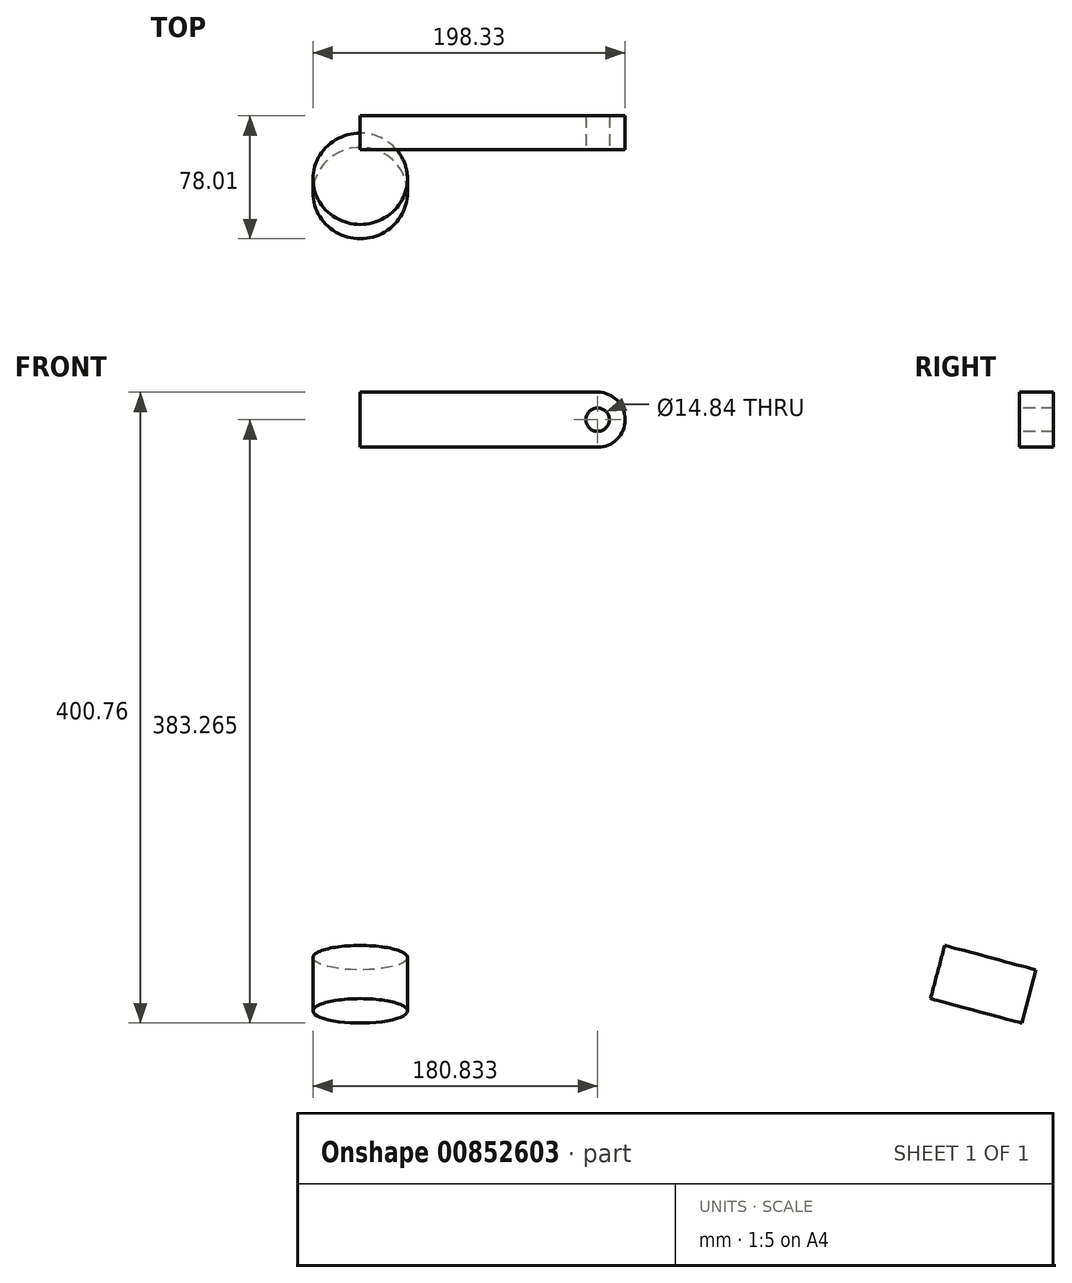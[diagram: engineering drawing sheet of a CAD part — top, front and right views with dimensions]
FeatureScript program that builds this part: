
annotation { "Feature Type Name" : "Feature", "Feature Type Description" : "" }
export const myFeature = defineFeature(function(context is Context, id is Id, definition is map)
    precondition{}
    {
        {
            var Q0;
            Q0=qCreatedBy(makeId("Front.planeOp"),FACE);
            var sketch = newSketch(context, id + "F0", { "sketchPlane" : qUnion([Q0])});
            skCircle(sketch, "E0", {"center": v(72.5, 0) * mm, "radius": 15 * mm});
            skCircle(sketch, "E1", {"center": v(95, 140) * mm, "radius": 15 * mm});
            skLineSegment(sketch, "E2.bottom", {"start": v(72.5, 15) * mm, "end": v(0, 15) * mm});
            skLineSegment(sketch, "E2.top", {"start": v(72.5, -15) * mm, "end": v(0, -15) * mm});
            skLineSegment(sketch, "E2.left", {"start": v(72.5, 15) * mm, "end": v(72.5, -15) * mm});
            skLineSegment(sketch, "E2.right", {"start": v(0, 15) * mm, "end": v(0, -15) * mm});
            skLineSegment(sketch, "E3.bottom", {"start": v(94.96, 125) * mm, "end": v(0, 125) * mm});
            skLineSegment(sketch, "E3.top", {"start": v(94.96, 155) * mm, "end": v(0, 155) * mm});
            skLineSegment(sketch, "E3.left", {"start": v(94.96, 155) * mm, "end": v(94.96, 125) * mm});
            skLineSegment(sketch, "E3.right", {"start": v(0, 155) * mm, "end": v(0, 125) * mm});
            skSolve(sketch);
        }
        {
            var Q0;
            {var subQ1=sQuery(id+"F0.wireOp",EDGE,"E3.bottom");Q0=makeQuery(id+"F0.imprint","IMPRINT",FACE,{"disambiguationData":[TD([[makeQuery(id+"F0.imprint","IMPRINT",EDGE,{"derivedFrom":subQ1}),1.0]])]});}
            var Q1;
            {var subQ4=sQuery(id+"F0.wireOp",EDGE,"E2.bottom");Q1=makeQuery(id+"F0.imprint","IMPRINT",FACE,{"disambiguationData":[TD([[makeQuery(id+"F0.imprint","IMPRINT",EDGE,{"derivedFrom":subQ4}),1.0]])]});}
            var Q2;
            {var subQ0=sQuery(id+"F0.wireOp",EDGE,"E3.left");var subQ1=sQuery(id+"F0.wireOp",EDGE,"E1");var subQ3=makeQuery(id+"F0.imprint","INTERSECT",VERTEX,{"derivedFrom":[subQ1,subQ0]});Q2=makeQuery(id+"F0.imprint","IMPRINT",FACE,{"disambiguationData":[TD([[makeQuery(id+"F0.imprint","IMPRINT",EDGE,{"disambiguationData":[TD([[subQ3,1.0]])],"derivedFrom":subQ1}),1.0]])]});}
            var Q3;
            {var subQ0=sQuery(id+"F0.wireOp",EDGE,"E3.left");var subQ1=sQuery(id+"F0.wireOp",EDGE,"E1");var subQ3=makeQuery(id+"F0.imprint","INTERSECT",VERTEX,{"derivedFrom":[subQ1,subQ0]});Q3=makeQuery(id+"F0.imprint","IMPRINT",FACE,{"disambiguationData":[TD([[makeQuery(id+"F0.imprint","IMPRINT",EDGE,{"disambiguationData":[TD([[subQ3,-1.0]])],"derivedFrom":subQ1}),1.0]])]});}
            var Q4;
            {var subQ0=sQuery(id+"F0.wireOp",EDGE,"E2.left");var subQ1=sQuery(id+"F0.wireOp",EDGE,"E0");var subQ3=makeQuery(id+"F0.imprint","INTERSECT",VERTEX,{"derivedFrom":[subQ1,subQ0]});Q4=makeQuery(id+"F0.imprint","IMPRINT",FACE,{"disambiguationData":[TD([[makeQuery(id+"F0.imprint","IMPRINT",EDGE,{"disambiguationData":[TD([[subQ3,1.0]])],"derivedFrom":subQ1}),1.0]])]});}
            var Q5;
            {var subQ0=sQuery(id+"F0.wireOp",EDGE,"E2.left");var subQ1=sQuery(id+"F0.wireOp",EDGE,"E0");var subQ3=makeQuery(id+"F0.imprint","INTERSECT",VERTEX,{"derivedFrom":[subQ1,subQ0]});Q5=makeQuery(id+"F0.imprint","IMPRINT",FACE,{"disambiguationData":[TD([[makeQuery(id+"F0.imprint","IMPRINT",EDGE,{"disambiguationData":[TD([[subQ3,-1.0]])],"derivedFrom":subQ1}),1.0]])]});}
            var Q6;
            {var subQ1=sQuery(id+"F0.wireOp",EDGE,"E3.bottom");Q6=makeQuery(id+"F0.imprint","IMPRINT",FACE,{"disambiguationData":[TD([[makeQuery(id+"F0.imprint","IMPRINT",EDGE,{"derivedFrom":subQ1}),-1.0]])]});}
            extrude(context, id + "F1", {"entities" : qUnion([Q0, Q1, Q2, Q3, Q4, Q5, Q6]), "depth" : 54 * mm, "offsetDistance" : 25 * mm});
        }
        {
            var Q0;
            {var subQ1=sQuery(id+"F0.wireOp",EDGE,"E3.bottom");Q0=makeQuery(id+"F0.imprint","IMPRINT",FACE,{"disambiguationData":[TD([[makeQuery(id+"F0.imprint","IMPRINT",EDGE,{"derivedFrom":subQ1}),1.0]])]});}
            var Q1;
            {var subQ0=sQuery(id+"F0.wireOp",EDGE,"E3.left");var subQ1=sQuery(id+"F0.wireOp",EDGE,"E1");var subQ3=makeQuery(id+"F0.imprint","INTERSECT",VERTEX,{"derivedFrom":[subQ1,subQ0]});Q1=makeQuery(id+"F0.imprint","IMPRINT",FACE,{"disambiguationData":[TD([[makeQuery(id+"F0.imprint","IMPRINT",EDGE,{"disambiguationData":[TD([[subQ3,1.0]])],"derivedFrom":subQ1}),1.0]])]});}
            var Q2;
            {var subQ0=sQuery(id+"F0.wireOp",EDGE,"E3.left");var subQ1=sQuery(id+"F0.wireOp",EDGE,"E1");var subQ3=makeQuery(id+"F0.imprint","INTERSECT",VERTEX,{"derivedFrom":[subQ1,subQ0]});Q2=makeQuery(id+"F0.imprint","IMPRINT",FACE,{"disambiguationData":[TD([[makeQuery(id+"F0.imprint","IMPRINT",EDGE,{"disambiguationData":[TD([[subQ3,-1.0]])],"derivedFrom":subQ1}),1.0]])]});}
            var Q3;
            {var subQ1=sQuery(id+"F0.wireOp",EDGE,"E3.bottom");Q3=makeQuery(id+"F0.imprint","IMPRINT",FACE,{"disambiguationData":[TD([[makeQuery(id+"F0.imprint","IMPRINT",EDGE,{"derivedFrom":subQ1}),-1.0]])]});}
            extrude(context, id + "F2", {"entities" : qUnion([Q0, Q1, Q2, Q3]), "oppositeDirection" : true, "depth" : 135 * mm, "offsetDistance" : 25 * mm});
        }
        {
            var Q0;
            {var subQ4=sQuery(id+"F0.wireOp",EDGE,"E2.bottom");Q0=makeQuery(id+"F0.imprint","IMPRINT",FACE,{"disambiguationData":[TD([[makeQuery(id+"F0.imprint","IMPRINT",EDGE,{"derivedFrom":subQ4}),1.0]])]});}
            var Q1;
            {var subQ0=sQuery(id+"F0.wireOp",EDGE,"E2.left");var subQ1=sQuery(id+"F0.wireOp",EDGE,"E0");var subQ3=makeQuery(id+"F0.imprint","INTERSECT",VERTEX,{"derivedFrom":[subQ1,subQ0]});Q1=makeQuery(id+"F0.imprint","IMPRINT",FACE,{"disambiguationData":[TD([[makeQuery(id+"F0.imprint","IMPRINT",EDGE,{"disambiguationData":[TD([[subQ3,1.0]])],"derivedFrom":subQ1}),1.0]])]});}
            var Q2;
            {var subQ0=sQuery(id+"F0.wireOp",EDGE,"E2.left");var subQ1=sQuery(id+"F0.wireOp",EDGE,"E0");var subQ3=makeQuery(id+"F0.imprint","INTERSECT",VERTEX,{"derivedFrom":[subQ1,subQ0]});Q2=makeQuery(id+"F0.imprint","IMPRINT",FACE,{"disambiguationData":[TD([[makeQuery(id+"F0.imprint","IMPRINT",EDGE,{"disambiguationData":[TD([[subQ3,-1.0]])],"derivedFrom":subQ1}),1.0]])]});}
            extrude(context, id + "F3", {"entities" : qUnion([Q0, Q1, Q2]), "oppositeDirection" : true, "depth" : 142 * mm, "offsetDistance" : 25 * mm});
        }
        {
            var Q0;
            Q0=makeQuery(id+"F2.opExtrude","CAP_FACE",FACE,{"disambiguationData":[OSD([sQuery(id+"F0.wireOp",EDGE,"E1"),sQuery(id+"F0.wireOp",EDGE,"E3.bottom"),sQuery(id+"F0.wireOp",EDGE,"E3.top"),sQuery(id+"F0.wireOp",EDGE,"E3.left"),sQuery(id+"F0.wireOp",EDGE,"E3.right")])],"isStart":false});
            extrude(context, id + "F4", {"entities" : qUnion([Q0]), "depth" : 54 * mm, "offsetDistance" : 25 * mm});
        }
        {
            var Q0;
            Q0=makeQuery(id+"F3.opExtrude","CAP_FACE",FACE,{"disambiguationData":[OSD([sQuery(id+"F0.wireOp",EDGE,"E0"),sQuery(id+"F0.wireOp",EDGE,"E2.bottom"),sQuery(id+"F0.wireOp",EDGE,"E2.top"),sQuery(id+"F0.wireOp",EDGE,"E2.left"),sQuery(id+"F0.wireOp",EDGE,"E2.right")])],"isStart":false});
            extrude(context, id + "F5", {"entities" : qUnion([Q0]), "depth" : 54 * mm, "offsetDistance" : 25 * mm});
        }
        {
            var Q0;
            Q0=qCreatedBy(makeId("Right.planeOp"),FACE);
            var sketch = newSketch(context, id + "F6", { "sketchPlane" : qUnion([Q0])});
            skLineSegment(sketch, "E4.bottom", {"start": v(81.76, 361.74) * mm, "end": v(60.24, 361.74) * mm});
            skLineSegment(sketch, "E4.top", {"start": v(81.76, 403.26) * mm, "end": v(60.24, 403.26) * mm});
            skLineSegment(sketch, "E4.left", {"start": v(81.76, 361.74) * mm, "end": v(81.76, 403.26) * mm});
            skLineSegment(sketch, "E4.right", {"start": v(60.24, 361.74) * mm, "end": v(60.24, 403.26) * mm});
            skPoint(sketch, "E4.middle", {"position": v(71, 382.5) * mm});
            skSolve(sketch);
        }
        {
            var Q0;
            Q0=makeQuery(id+"F6.imprint","IMPRINT",FACE,{"disambiguationData":[TD([[makeQuery(id+"F6.imprint","IMPRINT",EDGE,{"derivedFrom":sQuery(id+"F6.wireOp",EDGE,"E4.bottom")}),-1.0]])]});
            extrude(context, id + "F7", {"entities" : qUnion([Q0]), "depth" : 169 * mm, "offsetDistance" : 25 * mm});
        }
        {
            var Q0;
            Q0=makeQuery(id+"F7.opExtrude","SWEPT_FACE",FACE,{"disambiguationData":[OSD([sQuery(id+"F6.wireOp",EDGE,"E4.right")])]});
            var sketch = newSketch(context, id + "F8", { "sketchPlane" : qUnion([Q0])});
            skCircle(sketch, "E5", {"center": v(150.83, 381.74) * mm, "radius": 17.5 * mm});
            skCircle(sketch, "E6", {"center": v(150.83, 381.74) * mm, "radius": 7.42 * mm});
            skLineSegment(sketch, "E7.bottom", {"start": v(150.92, 399.23) * mm, "end": v(-0.78, 399.23) * mm});
            skLineSegment(sketch, "E7.top", {"start": v(150.92, 364.24) * mm, "end": v(-0.78, 364.24) * mm});
            skLineSegment(sketch, "E7.left", {"start": v(150.92, 399.23) * mm, "end": v(150.92, 364.24) * mm});
            skLineSegment(sketch, "E7.right", {"start": v(-0.78, 399.23) * mm, "end": v(-0.78, 364.24) * mm});
            skSolve(sketch);
        }
        {
            var Q0;
            {var subQ1=makeQuery(id+"F7.opExtrude","CAP_EDGE",EDGE,{"disambiguationData":[OSD([sQuery(id+"F6.wireOp",EDGE,"E4.right")])],"isStart":false});var subQ4=sQuery(id+"F8.wireOp",EDGE,"E6");var subQ5=makeQuery(id+"F8.imprint","INTERSECT",VERTEX,{"disambiguationData":[OD(0.0)],"derivedFrom":[subQ1,subQ4]});Q0=makeQuery(id+"F8.imprint","IMPRINT",FACE,{"disambiguationData":[TD([[makeQuery(id+"F8.imprint","IMPRINT",EDGE,{"disambiguationData":[TD([[subQ5,-1.0]])],"derivedFrom":subQ4}),-1.0]])]});}
            var Q1;
            {var subQ0=sQuery(id+"F8.wireOp",EDGE,"2KteYOMI-rCw2-rHk1-Q1Dc-6oNoVVmJXsEm");Q1=makeQuery(id+"F8.imprint","IMPRINT",FACE,{"disambiguationData":[TD([[makeQuery(id+"F8.imprint","IMPRINT",EDGE,{"derivedFrom":subQ0}),1.0]])]});}
            var Q2;
            {var subQ1=makeQuery(id+"F7.opExtrude","CAP_EDGE",EDGE,{"disambiguationData":[OSD([sQuery(id+"F6.wireOp",EDGE,"E4.right")])],"isStart":false});var subQ4=sQuery(id+"F8.wireOp",EDGE,"E6");var subQ5=makeQuery(id+"F8.imprint","INTERSECT",VERTEX,{"disambiguationData":[OD(0.0)],"derivedFrom":[subQ1,subQ4]});Q2=makeQuery(id+"F8.imprint","IMPRINT",FACE,{"disambiguationData":[TD([[makeQuery(id+"F8.imprint","IMPRINT",EDGE,{"disambiguationData":[TD([[subQ5,1.0]])],"derivedFrom":subQ4}),-1.0]])]});}
            var Q3;
            {var subQ0=sQuery(id+"F8.wireOp",EDGE,"E7.bottom");var subQ1=sQuery(id+"F8.wireOp",EDGE,"E5");var subQ2=makeQuery(id+"F8.imprint","INTERSECT",VERTEX,{"derivedFrom":[subQ1,subQ0]});Q3=makeQuery(id+"F8.imprint","IMPRINT",FACE,{"disambiguationData":[TD([[makeQuery(id+"F8.imprint","IMPRINT",EDGE,{"disambiguationData":[TD([[subQ2,-1.0]])],"derivedFrom":subQ1}),-1.0]])]});}
            extrude(context, id + "F9", {"entities" : qUnion([Q0, Q1, Q2, Q3]), "operationType" : NewBodyOperationType.INTERSECT, "oppositeDirection" : true, "depth" : 51 * mm, "offsetDistance" : 25 * mm});
        }
        {
            var Q0;
            Q0=sQuery(id+"F0.wireOp",EDGE,"E2.bottom");
            cPlane(context, id + "F10", {"entities" : qUnion([Q0]), "cplaneType" : CPlaneType.LINE_ANGLE, "offset" : 25 * mm, "angle" : 105 * degree, "width" : 150 * mm, "height" : 150 * mm});
        }
        {
            var Q0;
            Q0=qCreatedBy(id+"F10.planeOp",FACE);
            var sketch = newSketch(context, id + "F11", { "sketchPlane" : qUnion([Q0])});
            skCircle(sketch, "E8", {"center": v(0, 30) * mm, "radius": 30 * mm});
            skSolve(sketch);
        }
        {
            var Q0;
            Q0=makeQuery(id+"F11.imprint","IMPRINT",FACE,{"disambiguationData":[TD([[makeQuery(id+"F11.imprint","IMPRINT",EDGE,{"derivedFrom":sQuery(id+"F11.wireOp",EDGE,"E8")}),1.0]])]});
            extrude(context, id + "F12", {"entities" : qUnion([Q0]), "operationType" : NewBodyOperationType.ADD, "depth" : 35 * mm, "offsetDistance" : 25 * mm});
        }
    });
